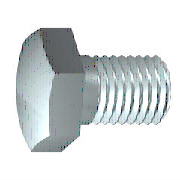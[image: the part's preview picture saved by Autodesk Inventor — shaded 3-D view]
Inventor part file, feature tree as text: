
AUTODESK INVENTOR PART (.ipt)
format: ipt  version: 2017 (Build 210142000, 142)  size: 194,560 bytes
history: native  units: mm (DEFAULTED — no unit token found)
features: sketch x2, extrude x1, chamfer x1, plane x1
ambient origin geometry x7: Origin, YZ Plane, XZ Plane, X Axis, Y Axis, Z Axis, Center Point
bodies: Solid1 (feature_tree), Body (feature_tree)
feature tree (5):
  extrude  "Head"  TaperAngle=90.0deg  [1 undecoded]
  chamfer  "Chamfer1"  [1 undecoded]
  plane  "Work Plane1"
  sketch  "Sketch1"  dims[d2=4.1656mm d12=90.0deg]
  sketch  "Sketch2"  dims[d3=2.794mm d4=0.0mm d21=90.0deg d6=0.39751mm d7=0.39761mm d8=0.0mm d11=6.35mm d15=31.26232mm d16=0.0mm d55=45.0deg d58=0.0mm d59=12.7mm d65=6.35mm d67=30.0deg d68=7.62mm d69=2.794mm d71=0.41656mm d73=0.0mm]
note: 2 required parameter values undecoded (feature->parameter linkage not recoverable at this tier; creation-order binding heuristic only, values carry confidence <= 0.55)
